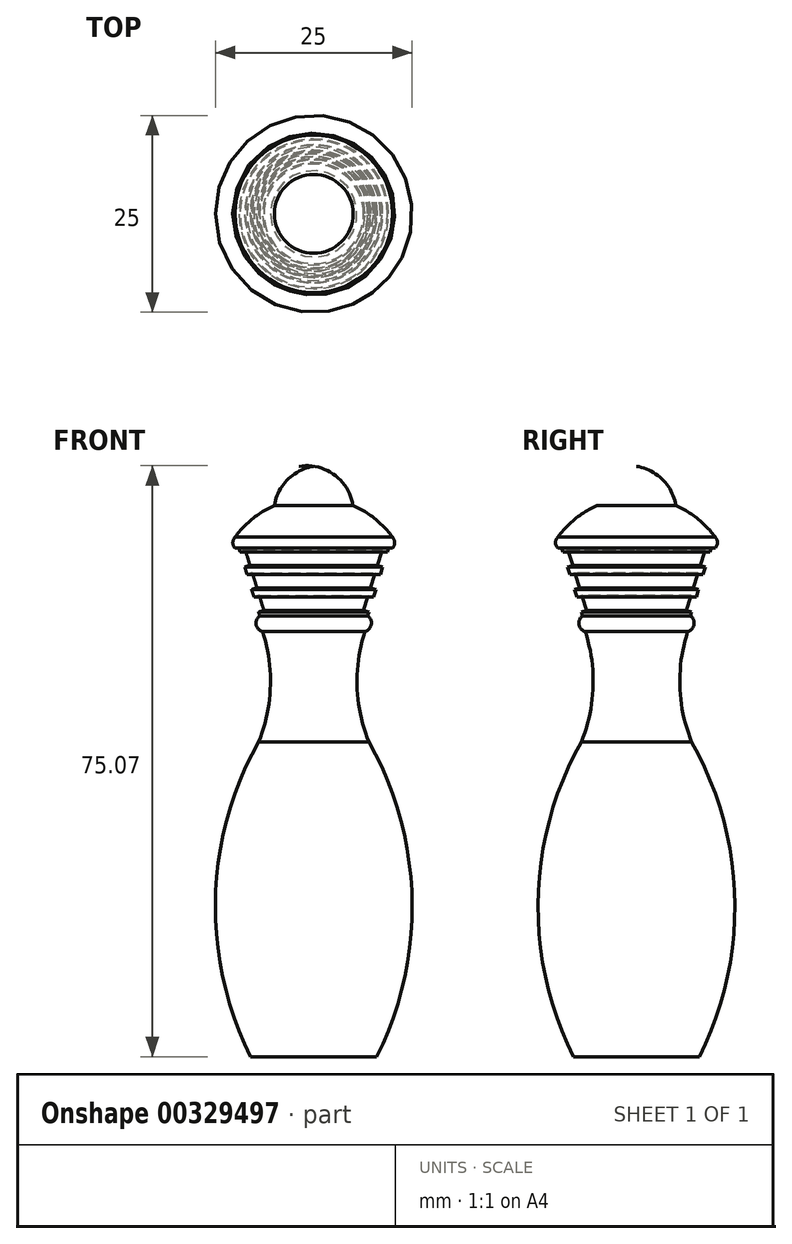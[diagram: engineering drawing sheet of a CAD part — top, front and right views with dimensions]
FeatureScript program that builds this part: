
annotation { "Feature Type Name" : "Feature", "Feature Type Description" : "" }
export const myFeature = defineFeature(function(context is Context, id is Id, definition is map)
    precondition{}
    {
        {
            var Q0;
            Q0=qCreatedBy(makeId("Front.planeOp"),FACE);
            var sketch = newSketch(context, id + "F0", { "sketchPlane" : qUnion([Q0])});
            skLineSegment(sketch, "E0", {"start": v(8, -75) * mm, "end": v(0, -75) * mm});
            skLineSegment(sketch, "E1", {"start": v(0, -75) * mm, "end": v(0, 0) * mm});
            skArc(sketch, "E2", {"start": v(5, -5) * mm, "mid": v(3.31, -1.69) * mm, "end": v(0, 0) * mm});
            skArc(sketch, "E3", {"start": v(10, -9) * mm, "mid": v(7.77, -6.66) * mm, "end": v(5, -5) * mm});
            skArc(sketch, "E4", {"start": v(10, -10.4) * mm, "mid": v(10.28, -9.7) * mm, "end": v(10, -9) * mm});
            skLineSegment(sketch, "E5", {"start": v(10, -10.4) * mm, "end": v(9.5, -10.4) * mm});
            skArc(sketch, "E6", {"start": v(8, -75) * mm, "mid": v(12.49, -54.88) * mm, "end": v(7, -35) * mm});
            skLineSegment(sketch, "E7", {"start": v(9.5, -10.4) * mm, "end": v(9.35, -10.88) * mm});
            skLineSegment(sketch, "E8", {"start": v(9.35, -10.88) * mm, "end": v(8.68, -10.67) * mm});
            skLineSegment(sketch, "E9", {"start": v(8.68, -10.67) * mm, "end": v(8.1, -12.58) * mm});
            skLineSegment(sketch, "E10", {"start": v(8.1, -12.58) * mm, "end": v(8.76, -12.79) * mm});
            skLineSegment(sketch, "E11", {"start": v(8.47, -13.74) * mm, "end": v(7.8, -13.54) * mm});
            skLineSegment(sketch, "E12", {"start": v(7.8, -13.54) * mm, "end": v(7.21, -15.45) * mm});
            skLineSegment(sketch, "E13", {"start": v(7.21, -15.45) * mm, "end": v(7.88, -15.65) * mm});
            skLineSegment(sketch, "E14", {"start": v(7.59, -16.61) * mm, "end": v(6.92, -16.4) * mm});
            skLineSegment(sketch, "E15", {"start": v(6.92, -16.4) * mm, "end": v(6.33, -18.32) * mm});
            skLineSegment(sketch, "E16", {"start": v(6.33, -18.32) * mm, "end": v(7, -18.52) * mm});
            skLineSegment(sketch, "E17.trimOffspring", {"start": v(8.76, -12.79) * mm, "end": v(8.47, -13.74) * mm});
            skLineSegment(sketch, "E18.trimOffspring", {"start": v(7.88, -15.65) * mm, "end": v(7.59, -16.61) * mm});
            skLineSegment(sketch, "E19.trimOffspring", {"start": v(7, -18.52) * mm, "end": v(6.85, -19) * mm});
            skArc(sketch, "E20", {"start": v(6.5, -21) * mm, "mid": v(5.51, -28.04) * mm, "end": v(7, -35) * mm});
            skArc(sketch, "E21", {"start": v(6.5, -21) * mm, "mid": v(7.31, -20.11) * mm, "end": v(6.85, -19) * mm});
            skSolve(sketch);
        }
        {
            var Q0;
            Q0=makeQuery(id+"F0.imprint","IMPRINT",FACE,{"disambiguationData":[TD([[makeQuery(id+"F0.imprint","IMPRINT",EDGE,{"derivedFrom":sQuery(id+"F0.wireOp",EDGE,"E0")}),-1.0]])]});
            var Q1;
            Q1=sQuery(id+"F0.wireOp",EDGE,"E1");
            revolve(context, id + "F1", {"entities" : qUnion([Q0]), "axis" : qUnion([Q1]), "revolveType" : RevolveType.FULL});
        }
    });
